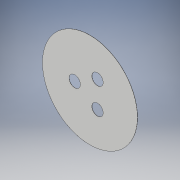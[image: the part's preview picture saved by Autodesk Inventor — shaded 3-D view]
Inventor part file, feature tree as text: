
AUTODESK INVENTOR PART (.ipt)
format: ipt  version: 2019 (Build 230136000, 136)  size: 113,664 bytes
history: native  units: mm
features: sketch x2, other x1, extrude x1, pattern_circular x1
ambient origin geometry x8: Origin, YZ Plane, XZ Plane, XY Plane, X Axis, Y Axis, Z Axis, Center Point
bodies: Body1 (feature_tree)
feature tree (5):
  other  "솔리드1"
  extrude  "돌출1"  Depth=250.0mm
  pattern_circular  "원형 패턴1"  [2 undecoded]
  sketch  "스케치1"
  sketch  "스케치2"
note: 2 required parameter values undecoded (feature->parameter linkage not recoverable at this tier; creation-order binding heuristic only, values carry confidence <= 0.55)
